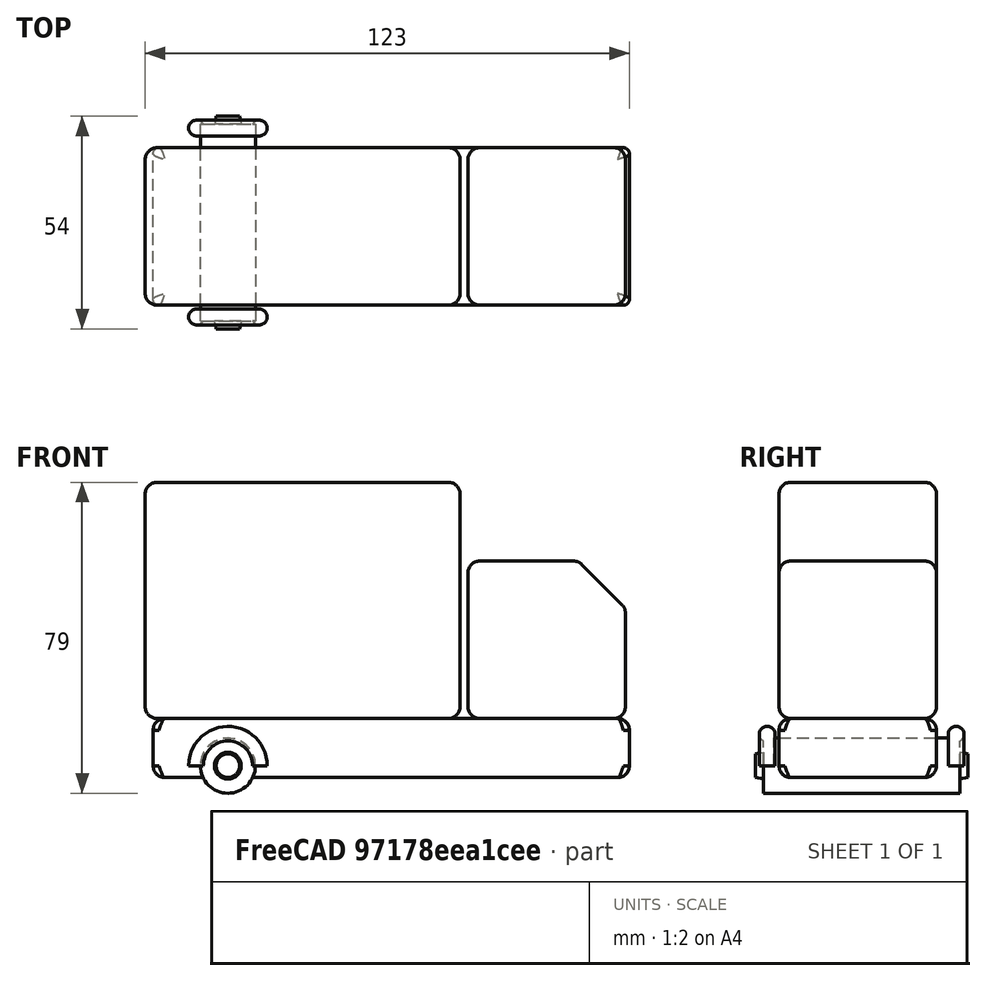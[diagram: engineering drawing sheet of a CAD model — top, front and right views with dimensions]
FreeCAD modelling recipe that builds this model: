
FCSTD DOCUMENT  (FreeCAD 0.21R33694 (Git))
Label: camoafdjhajk
License: All rights reserved
LicenseURL: http://en.wikipedia.org/wiki/All_rights_reserved
objects: Part::Fuse×6, Part::Box×4, Part::Fillet×4, Part::Torus×2, Part::Cone×2, Part::Cut×1, Part::Cylinder×1, Part::FeaturePython×1
note: 20 computed .brp shape members not serialized (recipe doc carries the construction recipe); baked Part::Feature solids carry a one-line shape summary decoded from their .brp

FEATURE [Part::Box] Box  label="Cube"
  AttacherType = Attacher::AttachEngine3D
  Height = 15
  Length = 121
  Width = 40
FEATURE [Part::Box] Box002  label="Cube002"
  AttacherType = Attacher::AttachEngine3D
  Height = 60
  Length = 80
  Placement = pos=(-2,0,15) rot=(0,0,1;0rad)
  Width = 40
FEATURE [Part::Box] Box003  label="Cube003"
  AttacherType = Attacher::AttachEngine3D
  Height = 40
  Length = 40
  Placement = pos=(60,0,15) rot=(0,0,1;0rad)
  Width = 40
FEATURE [Part::Box] Box004  label="Cube004"
  AttacherType = Attacher::AttachEngine3D
  Height = 40
  Length = 40
  Placement = pos=(102,0,41) rot=(0,-1,0;0.785398rad)
  Width = 40
FEATURE [Part::Cut] Cut
  Base = -> Box003
  Placement = pos=(20,0,0) rot=(0,0,1;0rad)
  Refine = true
  Tool = -> Box004
FEATURE [Part::Fillet] Fillet
  Base = -> Box
  Edges = 4 edges r=1.5: [Edge1,Edge3,Edge5,Edge7]
FEATURE [Part::Fillet] Fillet001  label="part de darrere"
  Base = -> Box002
  Edges = 12 edges r=3: [Edge1,Edge2,Edge3,Edge4,Edge5,Edge6,Edge7,Edge8,Edge9,Edge10,Edge11,Edge12]
FEATURE [Part::Fillet] Fillet002  label="part de dalt"
  Base = -> Cut
  Edges = 15 edges r=3: [Edge1,Edge2,Edge3,Edge4,Edge5,Edge6,Edge7,Edge8,Edge9,Edge10,Edge11,Edge12,Edge13,Edge14,Edge15]
FEATURE [Part::Fillet] Fillet003  label="base"
  Base = -> Fillet
  Edges = 16 edges r=3: [Edge1,Edge3,Edge5,Edge6,Edge7,Edge8,Edge9,Edge10,Edge11,Edge12,Edge14,Edge16,Edge17,Edge18,Edge19,Edge20]
FEATURE [Part::Cylinder] Cylinder  label="roda"
  Angle = 360
  AttacherType = Attacher::AttachEngine3D
  FirstAngle = 0
  Height = 50
  Placement = pos=(19,46,3) rot=(1,0,0;1.5708rad)
  Radius = 7
  SecondAngle = 0
FEATURE [Part::Torus] Torus  label="part_roda1"
  Angle1 = -180
  Angle2 = 180
  Angle3 = 180
  AttacherType = Attacher::AttachEngine3D
  Placement = pos=(19,-3,3) rot=(1,0,0;1.5708rad)
  Radius1 = 8
  Radius2 = 2
FEATURE [Part::Cone] Cone
  Angle = 360
  AttacherType = Attacher::AttachEngine3D
  Height = 10
  Placement = pos=(19,4,3) rot=(1,0,0;1.5708rad)
  Radius1 = 5
  Radius2 = 3
FEATURE [Part::Torus] Torus001  label="part_roda002"
  Angle1 = -180
  Angle2 = 180
  Angle3 = 180
  AttacherType = Attacher::AttachEngine3D
  Placement = pos=(19,45,3) rot=(1,0,0;1.5708rad)
  Radius1 = 8
  Radius2 = 2
FEATURE [Part::Cone] Cone001
  Angle = 360
  AttacherType = Attacher::AttachEngine3D
  Height = 10
  Placement = pos=(19,48,3) rot=(1,0,0;1.5708rad)
  Radius1 = 3
  Radius2 = 5
FEATURE [Part::Fuse] Fusion
  Base = -> Cylinder
  Refine = true
  Tool = -> Torus
FEATURE [Part::Fuse] Fusion001
  Base = -> Cone001
  Refine = true
  Tool = -> Fusion
FEATURE [Part::Fuse] Fusion002
  Base = -> Torus001
  Refine = true
  Tool = -> Fusion001
FEATURE [Part::Fuse] Fusion003  label="Roda1"
  Base = -> Cone
  Refine = true
  Tool = -> Fusion002
FEATURE [Part::FeaturePython] Array  label="rodes"  # Draft array (typed FeaturePython)
  AlwaysSyncPlacement = false
  Angle = 360
  ArrayType = 0
  Axis = (0,0,1)
  Base = -> Fusion003
  Center = (0,0,0)
  Count = 4
  ExpandArray = false
  Fuse = false
  IntervalAxis = (0,0,0)
  IntervalX = (25,0,0)
  IntervalY = (0,100,0)
  IntervalZ = (0,0,100)
  NumberCircles = 3
  NumberPolar = 5
  NumberX = 4
  NumberY = 1
  NumberZ = 1
  PlacementList = 4 placements: arithmetic series from (0,0,0) step (25,0,0) to (75,0,0)
  RadialDistance = 50
  ScaleList = (4) [(1,1,1),(1,1,1),(1,1,1),(1,1,1)]
  Symmetry = 1
  TangentialDistance = 25
FEATURE [Part::Fuse] Fusion004
  Base = -> Fillet001
  Refine = true
  Tool = -> Fillet002
FEATURE [Part::Fuse] Fusion005
  Base = -> Fillet001
  Refine = true
  Tool = -> Fillet002
